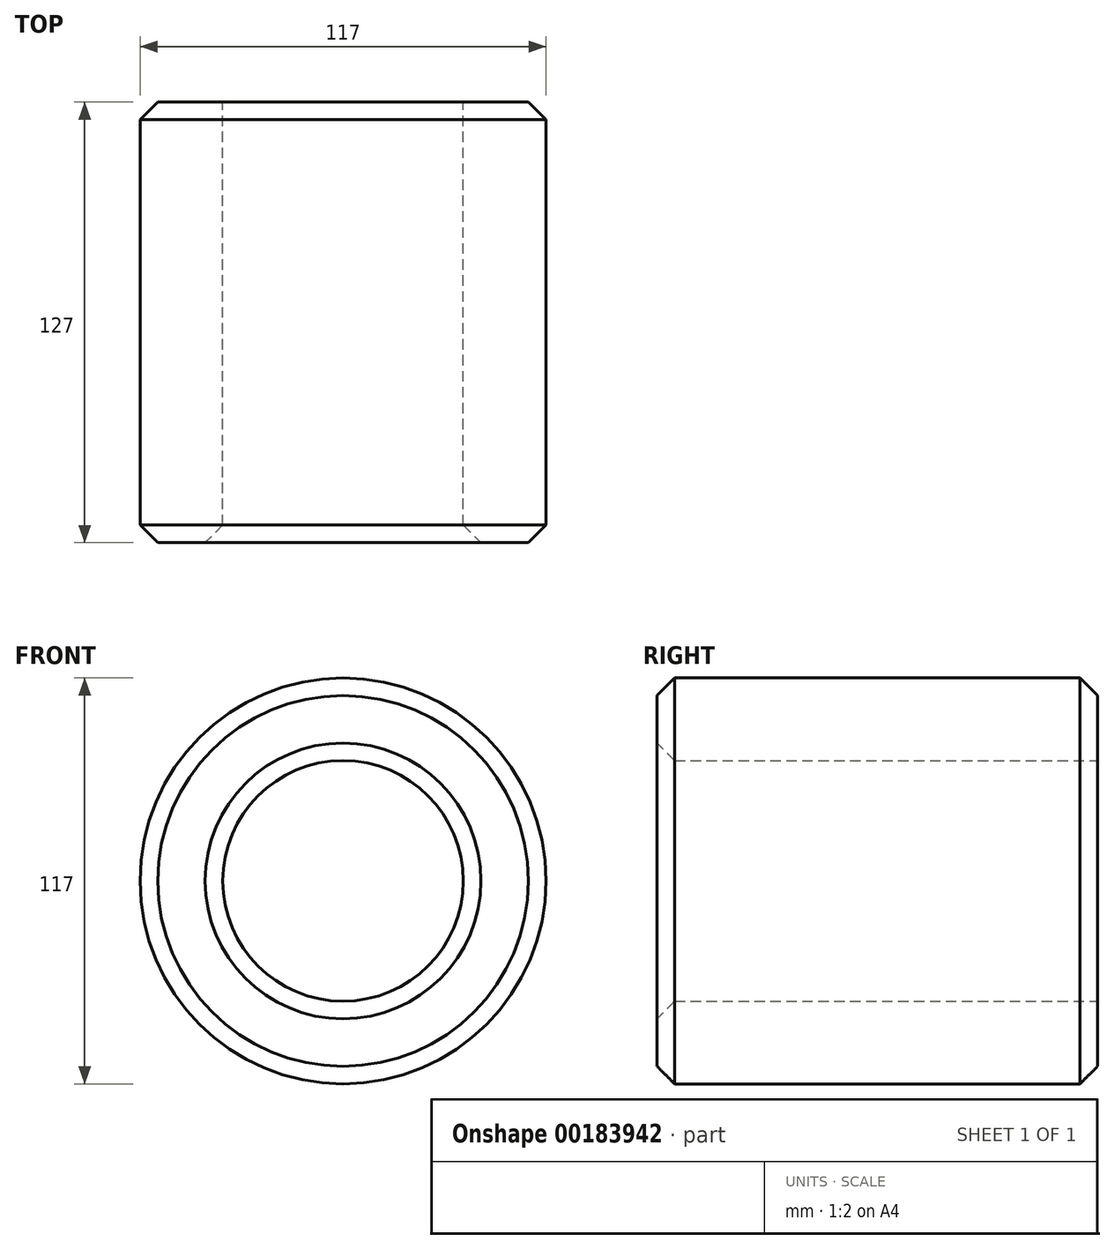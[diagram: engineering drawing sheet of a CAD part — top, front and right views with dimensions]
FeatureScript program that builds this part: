
annotation { "Feature Type Name" : "Feature", "Feature Type Description" : "" }
export const myFeature = defineFeature(function(context is Context, id is Id, definition is map)
    precondition{}
    {
        {
            var Q0;
            Q0=qCreatedBy(makeId("Front.planeOp"),FACE);
            var sketch = newSketch(context, id + "F0", { "sketchPlane" : qUnion([Q0])});
            skCircle(sketch, "E0", {"center": v(0, 0) * mm, "radius": 58.5 * mm});
            skSolve(sketch);
        }
        {
            var Q0;
            Q0=makeQuery(id+"F0.imprint","IMPRINT",FACE,{"disambiguationData":[TD([[makeQuery(id+"F0.imprint","IMPRINT",EDGE,{"derivedFrom":sQuery(id+"F0.wireOp",EDGE,"E0")}),1.0]])]});
            extrude(context, id + "F1", {"entities" : qUnion([Q0]), "depth" : 127 * mm});
        }
        {
            var Q0;
            Q0=makeQuery(id+"F1.opExtrude","CAP_FACE",FACE,{"disambiguationData":[OSD([sQuery(id+"F0.wireOp",EDGE,"E0")])],"isStart":true});
            var sketch = newSketch(context, id + "F2", { "sketchPlane" : qUnion([Q0])});
            skCircle(sketch, "E1", {"center": v(0, 0) * mm, "radius": 34.67 * mm});
            skSolve(sketch);
        }
        {
            var Q0;
            Q0 = qSketchRegion(id + "F2", true);
            extrude(context, id + "F3", {"entities" : qUnion([Q0]), "operationType" : NewBodyOperationType.REMOVE, "endBound" : BoundingType.THROUGH_ALL, "oppositeDirection" : true, "depth" : 25.4 * mm});
        }
        {
            var Q0;
            Q0=makeQuery(id+"F1.opExtrude","CAP_EDGE",EDGE,{"disambiguationData":[OSD([sQuery(id+"F0.wireOp",EDGE,"E0")])],"isStart":true});
            var Q1;
            Q1=makeQuery(id+"F3.boolean.opBoolean","COPY",EDGE,{"derivedFrom":makeQuery(id+"F3.opExtrude","CAP_EDGE",EDGE,{"disambiguationData":[OSD([sQuery(id+"F2.wireOp",EDGE,"E1")])],"isStart":true})});
            var Q2;
            Q2=makeQuery(id+"F1.opExtrude","CAP_EDGE",EDGE,{"disambiguationData":[OSD([sQuery(id+"F0.wireOp",EDGE,"E0")])],"isStart":false});
            var Q3;
            Q3=makeQuery(id+"F3.boolean.opBoolean","INTERSECT",EDGE,{"derivedFrom":[makeQuery(id+"F1.opExtrude","CAP_FACE",FACE,{"disambiguationData":[OSD([sQuery(id+"F0.wireOp",EDGE,"E0")])],"isStart":false}),makeQuery(id+"F3.opExtrude","SWEPT_FACE",FACE,{"disambiguationData":[OSD([sQuery(id+"F2.wireOp",EDGE,"E1")])]})]});
            chamfer(context, id + "F4", {"entities" : qUnion([Q0, Q1, Q2, Q3]), "width" : 5.08 * mm, "tangentPropagation" : true});
        }
    });
